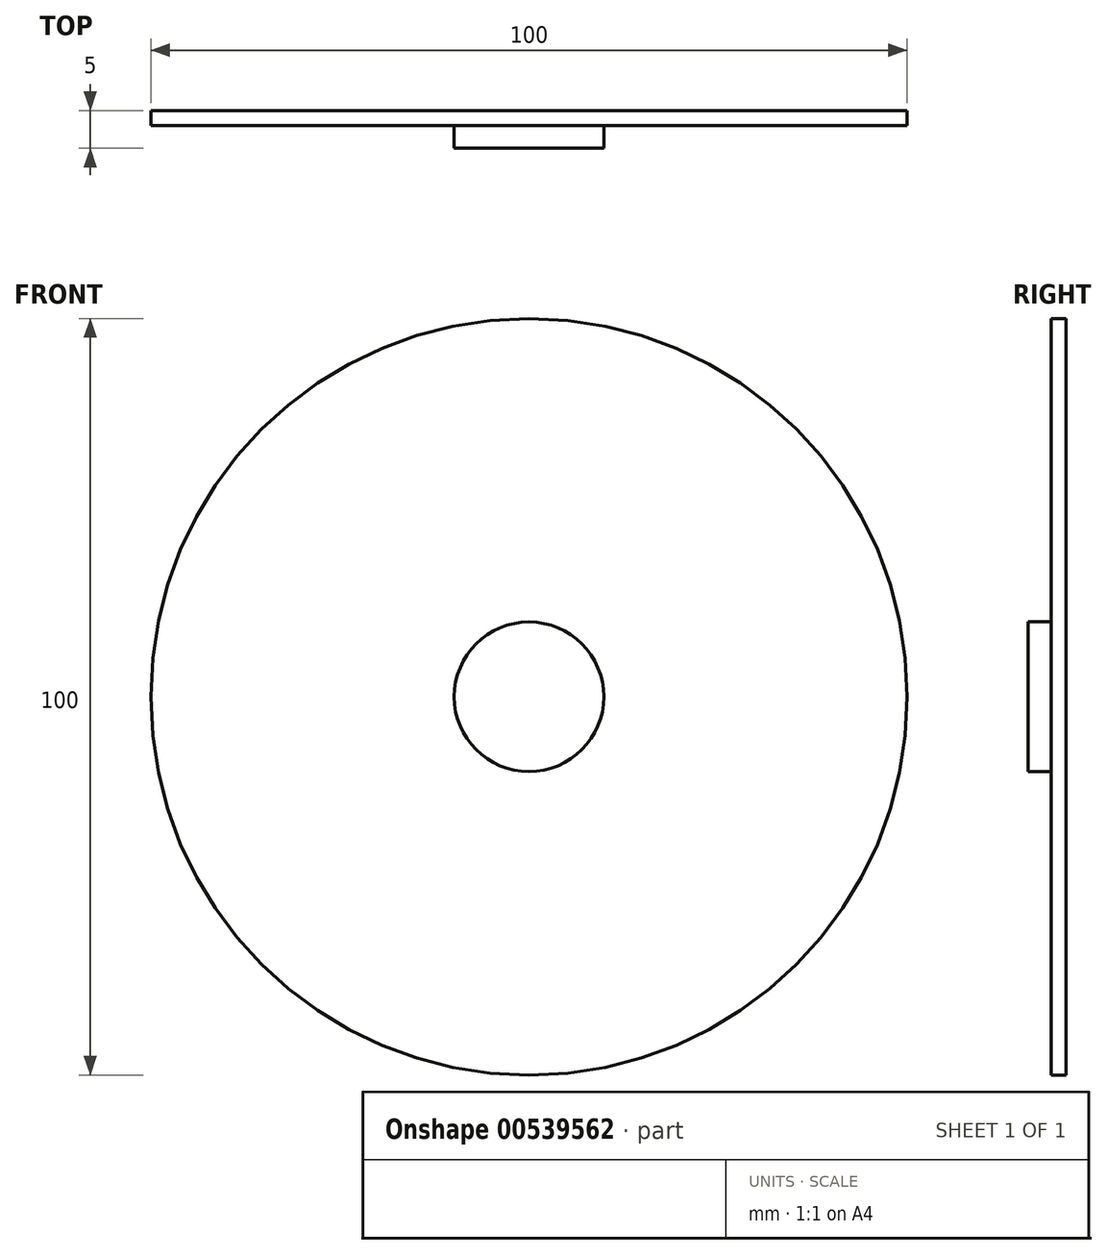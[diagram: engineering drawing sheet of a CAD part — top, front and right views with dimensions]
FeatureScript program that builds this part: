
annotation { "Feature Type Name" : "Feature", "Feature Type Description" : "" }
export const myFeature = defineFeature(function(context is Context, id is Id, definition is map)
    precondition{}
    {
        {
            var Q0;
            Q0=qCreatedBy(makeId("Front.planeOp"),FACE);
            var sketch = newSketch(context, id + "F0", { "sketchPlane" : qUnion([Q0])});
            skCircle(sketch, "E0", {"center": v(0, 0) * mm, "radius": 50 * mm});
            skSolve(sketch);
        }
        {
            var Q0;
            Q0 = qSketchRegion(id + "F0", true);
            extrude(context, id + "F1", {"entities" : qUnion([Q0]), "depth" : 2 * mm, "offsetDistance" : 25 * mm});
        }
        {
            var Q0;
            Q0=qCreatedBy(makeId("Front.planeOp"),FACE);
            var sketch = newSketch(context, id + "F2", { "sketchPlane" : qUnion([Q0])});
            skCircle(sketch, "E1", {"center": v(0, 0) * mm, "radius": 9.89 * mm});
            skSolve(sketch);
        }
        {
            var Q0;
            Q0 = qSketchRegion(id + "F2", true);
            extrude(context, id + "F3", {"entities" : qUnion([Q0]), "operationType" : NewBodyOperationType.ADD, "depth" : 5 * mm, "offsetDistance" : 25 * mm});
        }
    });
